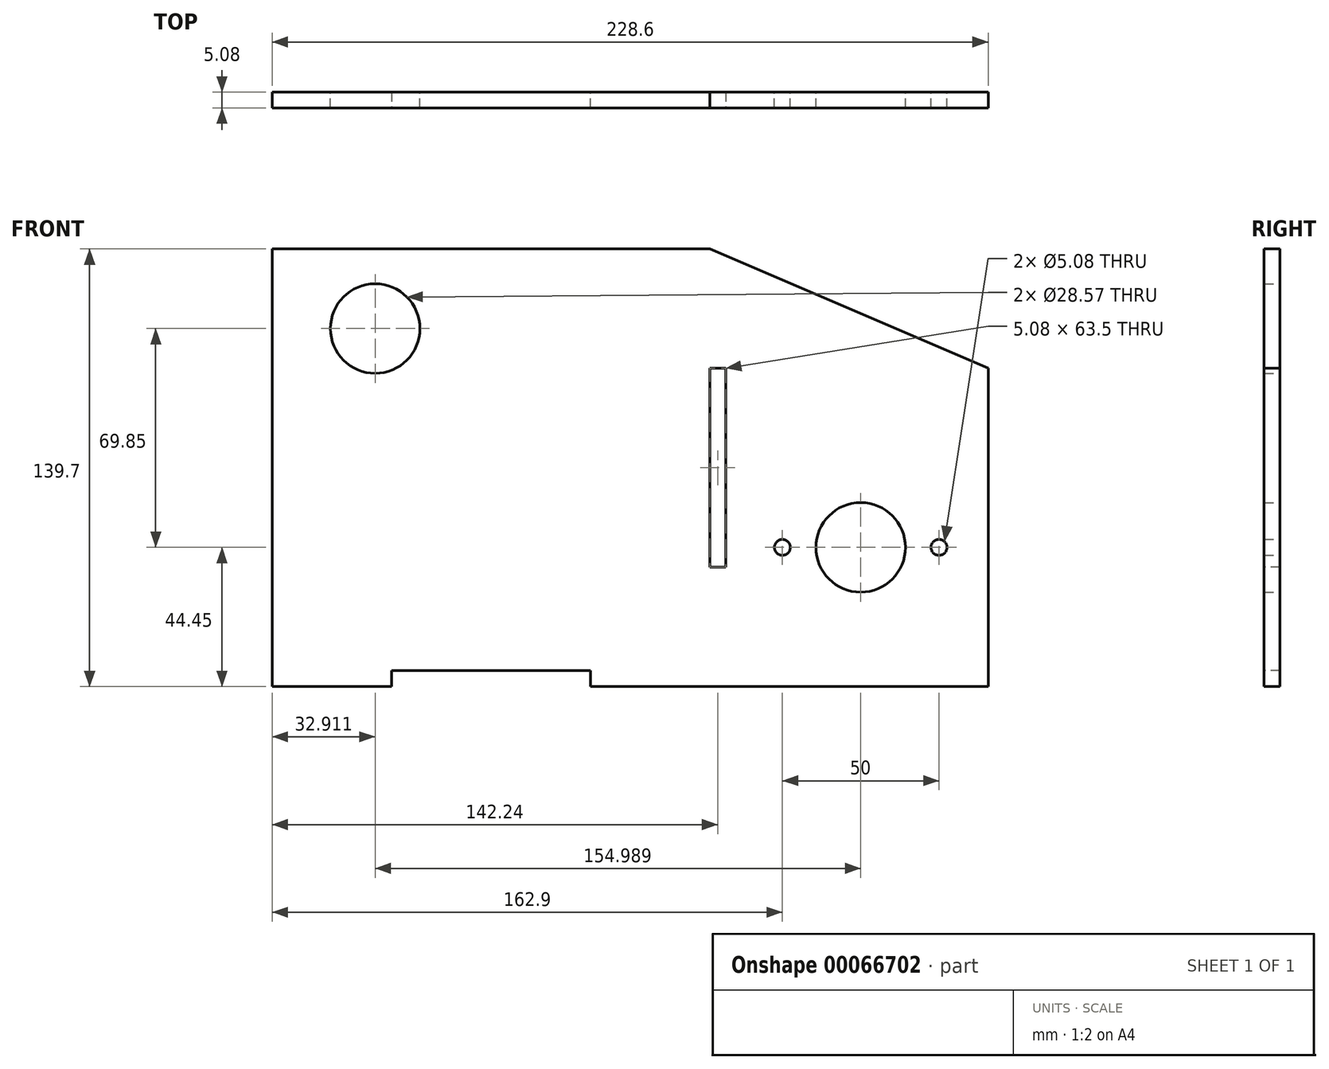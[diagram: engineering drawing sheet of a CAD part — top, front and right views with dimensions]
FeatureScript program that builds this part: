
annotation { "Feature Type Name" : "Feature", "Feature Type Description" : "" }
export const myFeature = defineFeature(function(context is Context, id is Id, definition is map)
    precondition{}
    {
        {
            var Q0;
            Q0=qCreatedBy(makeId("Front.planeOp"),FACE);
            var sketch = newSketch(context, id + "F0", { "sketchPlane" : qUnion([Q0])});
            skLineSegment(sketch, "E0", {"start": v(0, 0) * mm, "end": v(228.6, 0) * mm});
            skLineSegment(sketch, "E1", {"start": v(228.6, 0) * mm, "end": v(228.6, -139.7) * mm});
            skLineSegment(sketch, "E2", {"start": v(228.6, -139.7) * mm, "end": v(139.7, -139.7) * mm});
            skLineSegment(sketch, "E3", {"start": v(139.7, -139.7) * mm, "end": v(0, -139.7) * mm});
            skLineSegment(sketch, "E4", {"start": v(0, -139.7) * mm, "end": v(0, 0) * mm});
            skLineSegment(sketch, "E5", {"start": v(228.6, 0) * mm, "end": v(190.5, 0) * mm});
            skCircle(sketch, "E6", {"center": v(187.9, -95.25) * mm, "radius": 14.29 * mm});
            skLineSegment(sketch, "E7", {"start": v(162.9, -95.25) * mm, "end": v(212.9, -95.25) * mm});
            skCircle(sketch, "E8", {"center": v(162.9, -95.25) * mm, "radius": 2.54 * mm});
            skCircle(sketch, "E9", {"center": v(212.9, -95.25) * mm, "radius": 2.54 * mm});
            skLineSegment(sketch, "E10", {"start": v(0, -25.4) * mm, "end": v(32.91, -25.4) * mm});
            skLineSegment(sketch, "E11", {"start": v(32.91, 0) * mm, "end": v(32.91, -25.4) * mm});
            skCircle(sketch, "E12", {"center": v(32.91, -25.4) * mm, "radius": 14.29 * mm});
            skLineSegment(sketch, "E13", {"start": v(228.6, -139.7) * mm, "end": v(228.6, -38.1) * mm});
            skLineSegment(sketch, "E14", {"start": v(0, 0) * mm, "end": v(139.7, 0) * mm});
            skLineSegment(sketch, "E15", {"start": v(139.7, 0) * mm, "end": v(228.6, -38.1) * mm});
            skLineSegment(sketch, "E16", {"start": v(32.91, -25.4) * mm, "end": v(187.9, -95.25) * mm});
            skLineSegment(sketch, "E17", {"start": v(187.9, -139.7) * mm, "end": v(187.9, -95.25) * mm});
            skSolve(sketch);
        }
        {
            var Q0;
            {var subQ0=sQuery(id+"F0.wireOp",EDGE,"E14");var subQ6=sQuery(id+"F0.wireOp",EDGE,"E4");var subQ9=makeQuery(id+"F0.imprint","INTERSECT",VERTEX,{"derivedFrom":[subQ6,subQ0]});Q0=makeQuery(id+"F0.imprint","IMPRINT",FACE,{"disambiguationData":[TD([[makeQuery(id+"F0.imprint","IMPRINT",EDGE,{"disambiguationData":[TD([[subQ9,1.0]])],"derivedFrom":subQ6}),-1.0]])]});}
            var Q1;
            Q1=makeQuery(id+"F0.imprint","IMPRINT",FACE,{"disambiguationData":[TD([[makeQuery(id+"F0.imprint","IMPRINT",EDGE,{"derivedFrom":sQuery(id+"F0.wireOp",EDGE,"E2")}),-1.0]])]});
            var Q2;
            Q2=makeQuery(id+"F0.imprint","IMPRINT",FACE,{"disambiguationData":[TD([[makeQuery(id+"F0.imprint","IMPRINT",EDGE,{"derivedFrom":sQuery(id+"F0.wireOp",EDGE,"E9")}),-1.0]])]});
            extrude(context, id + "F1", {"entities" : qUnion([Q0, Q1, Q2]), "depth" : 5.08 * mm});
        }
        {
            var Q0;
            Q0=makeQuery(id+"F1.opExtrude","SWEPT_FACE",FACE,{"disambiguationData":[OSD([sQuery(id+"F0.wireOp",EDGE,"E3")])]});
            var sketch = newSketch(context, id + "F2", { "sketchPlane" : qUnion([Q0])});
            skLineSegment(sketch, "E18.bottom", {"start": v(0, 0) * mm, "end": v(38.1, 0) * mm});
            skLineSegment(sketch, "E18.top", {"start": v(0, 5.08) * mm, "end": v(38.1, 5.08) * mm});
            skLineSegment(sketch, "E18.left", {"start": v(0, 0) * mm, "end": v(0, 5.08) * mm});
            skLineSegment(sketch, "E18.right", {"start": v(38.1, 0) * mm, "end": v(38.1, 5.08) * mm});
            skLineSegment(sketch, "E19", {"start": v(0, 5.08) * mm, "end": v(101.6, 5.08) * mm});
            skLineSegment(sketch, "E20", {"start": v(101.6, 5.08) * mm, "end": v(101.6, 0) * mm});
            skLineSegment(sketch, "E21", {"start": v(101.6, 0) * mm, "end": v(38.1, 0) * mm});
            skSolve(sketch);
        }
        {
            var Q0;
            {var subQ0=sQuery(id+"F2.wireOp",EDGE,"E18.right");Q0=makeQuery(id+"F2.imprint","IMPRINT",FACE,{"disambiguationData":[TD([[makeQuery(id+"F2.imprint","IMPRINT",EDGE,{"derivedFrom":subQ0}),-1.0]])]});}
            extrude(context, id + "F3", {"entities" : qUnion([Q0]), "operationType" : NewBodyOperationType.REMOVE, "oppositeDirection" : true, "depth" : 5.08 * mm});
        }
        {
            var Q0;
            Q0=makeQuery(id+"F1.opExtrude","CAP_FACE",FACE,{"disambiguationData":[OSD([sQuery(id+"F0.wireOp",EDGE,"E0"),sQuery(id+"F0.wireOp",EDGE,"E1"),sQuery(id+"F0.wireOp",EDGE,"E2"),sQuery(id+"F0.wireOp",EDGE,"E3"),sQuery(id+"F0.wireOp",EDGE,"E4"),sQuery(id+"F0.wireOp",EDGE,"E5"),sQuery(id+"F0.wireOp",EDGE,"E6"),sQuery(id+"F0.wireOp",EDGE,"E8"),sQuery(id+"F0.wireOp",EDGE,"E9"),sQuery(id+"F0.wireOp",EDGE,"E12")])],"isStart":false});
            var sketch = newSketch(context, id + "F4", { "sketchPlane" : qUnion([Q0])});
            skLineSegment(sketch, "E22", {"start": v(139.7, -101.6) * mm, "end": v(144.78, -101.6) * mm});
            skLineSegment(sketch, "E23", {"start": v(139.7, -38.1) * mm, "end": v(144.78, -38.1) * mm});
            skLineSegment(sketch, "E24", {"start": v(139.7, -69.85) * mm, "end": v(0, -69.85) * mm});
            skLineSegment(sketch, "E25", {"start": v(139.7, -38.1) * mm, "end": v(139.7, -101.6) * mm});
            skLineSegment(sketch, "E26", {"start": v(142.24, -101.6) * mm, "end": v(142.24, -139.7) * mm});
            skLineSegment(sketch, "E27", {"start": v(144.78, -38.1) * mm, "end": v(144.78, -101.6) * mm});
            skSolve(sketch);
        }
        {
            var Q0;
            {var subQ0=sQuery(id+"F4.wireOp",EDGE,"E22");Q0=makeQuery(id+"F4.imprint","IMPRINT",FACE,{"disambiguationData":[TD([[makeQuery(id+"F4.imprint","IMPRINT",EDGE,{"derivedFrom":subQ0}),1.0]])]});}
            extrude(context, id + "F5", {"entities" : qUnion([Q0]), "operationType" : NewBodyOperationType.REMOVE, "oppositeDirection" : true, "depth" : 25.4 * mm});
        }
    });
